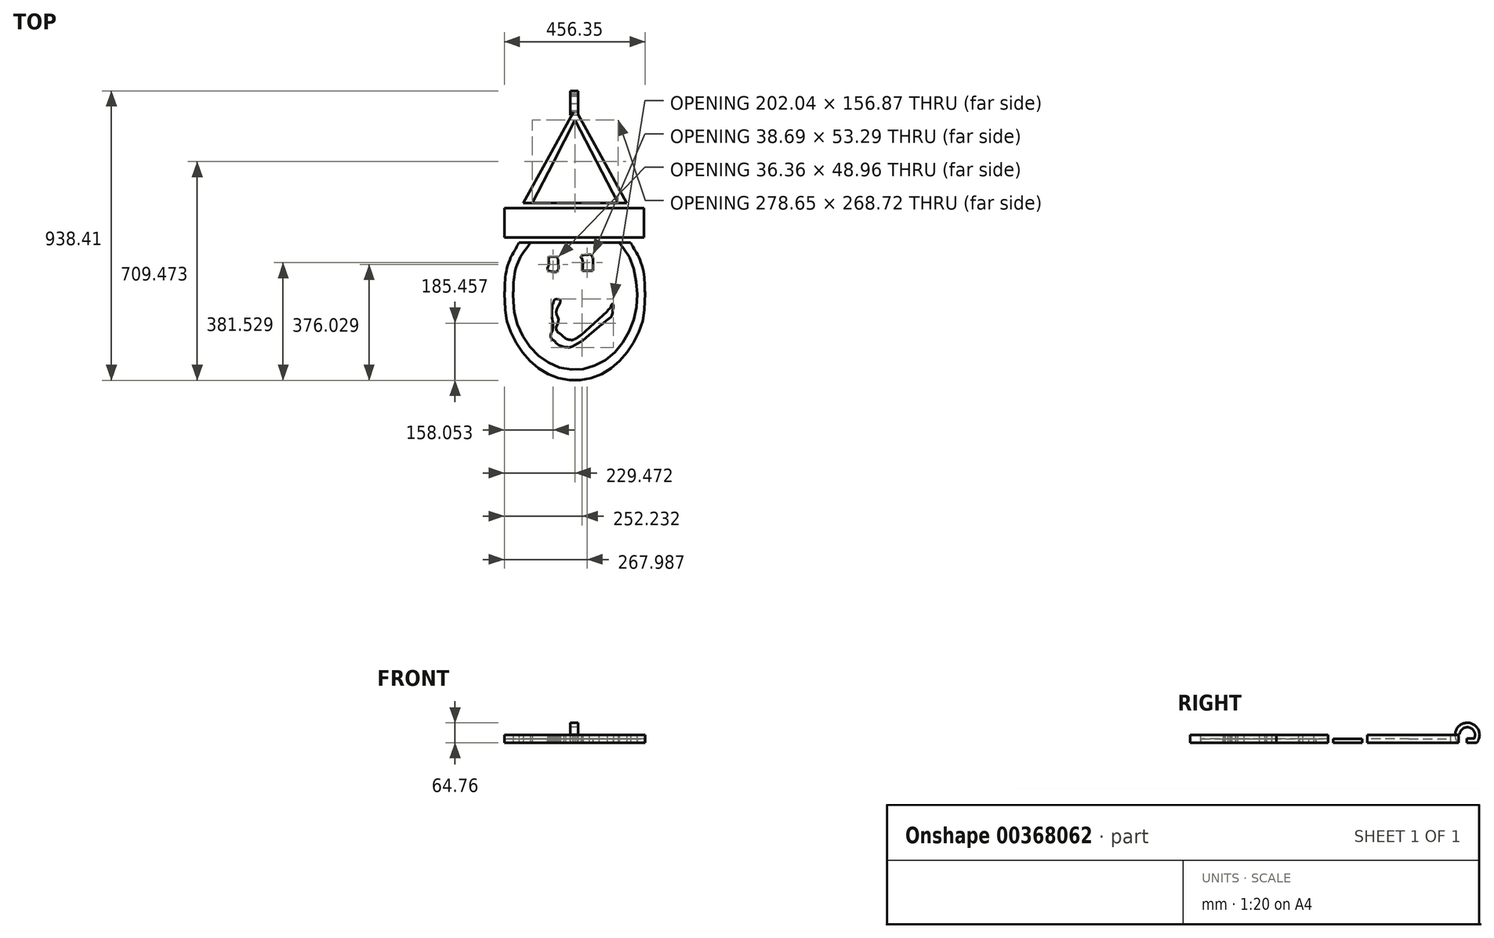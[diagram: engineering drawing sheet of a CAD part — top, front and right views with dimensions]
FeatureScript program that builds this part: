
annotation { "Feature Type Name" : "Feature", "Feature Type Description" : "" }
export const myFeature = defineFeature(function(context is Context, id is Id, definition is map)
    precondition{}
    {
        {
            var Q0;
            Q0=qCreatedBy(makeId("Top.planeOp"),FACE);
            var sketch = newSketch(context, id + "F0", { "sketchPlane" : qUnion([Q0])});
            skFitSpline(sketch, "E0", {"points": [v(-178.82, 5.14) * mm, v(-188.06, -11.68) * mm, v(-206.77, -45.7) * mm, v(-222.61, -102.94) * mm, v(-224.79, -142.5) * mm, v(-225.89, -162.5) * mm]});
            skFitSpline(sketch, "E1", {"points": [v(-225.89, -162.5) * mm, v(-224.4, -186.57) * mm, v(-221.45, -234.01) * mm, v(-198.02, -300.85) * mm, v(-162.12, -358.66) * mm, v(-114.52, -403.46) * mm, v(-58.59, -431.98) * mm, v(1.96, -441.82) * mm, v(62.51, -431.99) * mm, v(118.45, -403.48) * mm, v(166.06, -358.67) * mm, v(201.97, -300.87) * mm, v(225.41, -234.02) * mm, v(228.35, -186.57) * mm, v(229.85, -162.5) * mm]});
            skLineSegment(sketch, "E2", {"start": v(3, 438.57) * mm, "end": v(-88.01, 272.71) * mm});
            skLineSegment(sketch, "E3", {"start": v(-88.01, 272.71) * mm, "end": v(-164.6, 133.21) * mm});
            skLineSegment(sketch, "E4", {"start": v(-164.6, 133.21) * mm, "end": v(170.6, 133.21) * mm});
            skLineSegment(sketch, "E5", {"start": v(170.6, 133.21) * mm, "end": v(94, 272.71) * mm});
            skLineSegment(sketch, "E6", {"start": v(94, 272.71) * mm, "end": v(3, 438.57) * mm});
            skFitSpline(sketch, "E7", {"points": [v(229.85, -162.5) * mm, v(228.74, -142.5) * mm, v(226.54, -102.93) * mm, v(210.65, -45.68) * mm, v(191.92, -11.67) * mm, v(182.66, 5.14) * mm]});
            skFitSpline(sketch, "E8", {"points": [v(-141.9, 5.14) * mm, v(-152.88, -10.94) * mm, v(-175.16, -43.58) * mm, v(-194.2, -101.44) * mm, v(-196.82, -141.96) * mm, v(-198.14, -162.5) * mm]});
            skLineSegment(sketch, "E9", {"start": v(182.66, 5.14) * mm, "end": v(-178.82, 5.14) * mm});
            skLineSegment(sketch, "E10", {"start": v(146.1, 5.14) * mm, "end": v(-141.9, 5.14) * mm});
            skLineSegment(sketch, "E11", {"start": v(-244.23, 133.2) * mm, "end": v(244.23, 133.2) * mm});
            skLineSegment(sketch, "E12", {"start": v(244.23, 133.2) * mm, "end": v(244.23, 5.13) * mm});
            skLineSegment(sketch, "E13", {"start": v(244.23, 5.13) * mm, "end": v(-244.23, 5.13) * mm});
            skLineSegment(sketch, "E14", {"start": v(-244.23, 5.13) * mm, "end": v(-244.23, 133.2) * mm});
            skLineSegment(sketch, "E15", {"start": v(3, 402.01) * mm, "end": v(-66.66, 267.63) * mm});
            skLineSegment(sketch, "E16", {"start": v(-66.66, 267.63) * mm, "end": v(-136.35, 133.3) * mm});
            skLineSegment(sketch, "E17", {"start": v(-136.35, 133.3) * mm, "end": v(3, 133.3) * mm});
            skLineSegment(sketch, "E18", {"start": v(3, 133.3) * mm, "end": v(142.3, 133.3) * mm});
            skLineSegment(sketch, "E19", {"start": v(142.3, 133.3) * mm, "end": v(72.64, 267.63) * mm});
            skLineSegment(sketch, "E20", {"start": v(72.64, 267.63) * mm, "end": v(3, 402.01) * mm});
            skFitSpline(sketch, "E21", {"points": [v(-198.14, -162.5) * mm, v(-196.83, -183.58) * mm, v(-194.25, -225.14) * mm, v(-173.66, -283.68) * mm, v(-142.13, -334.3) * mm, v(-100.31, -373.54) * mm, v(-51.2, -398.5) * mm, v(1.96, -407.13) * mm, v(55.12, -398.5) * mm, v(104.24, -373.54) * mm, v(146, -334.3) * mm, v(177.74, -283.68) * mm, v(197.56, -225.15) * mm, v(204.33, -162.98) * mm, v(197.62, -101.48) * mm, v(179.39, -43.61) * mm, v(157.1, -10.95) * mm, v(146.1, 5.14) * mm]});
            skLineSegment(sketch, "E22", {"start": v(-226.5, 116.41) * mm, "end": v(226.5, 116.41) * mm});
            skLineSegment(sketch, "E23", {"start": v(226.5, 116.41) * mm, "end": v(226.5, 21.92) * mm});
            skLineSegment(sketch, "E24", {"start": v(226.5, 21.92) * mm, "end": v(-226.5, 21.92) * mm});
            skLineSegment(sketch, "E25", {"start": v(-226.5, 21.92) * mm, "end": v(-226.5, 116.41) * mm});
            skFitSpline(sketch, "E26", {"points": [v(-71.66, -200.42) * mm, v(-71.94, -212.65) * mm, v(-72.5, -237.2) * mm, v(-69, -272.4) * mm, v(-76.01, -299.15) * mm, v(-68.45, -311.04) * mm, v(-65.86, -312.06) * mm, v(-64.26, -312.62) * mm, v(-63.72, -312.81) * mm]});
            skLineSegment(sketch, "E27", {"start": v(-63.72, -312.81) * mm, "end": v(-59.91, -319.8) * mm});
            skLineSegment(sketch, "E28", {"start": v(-59.91, -319.8) * mm, "end": v(-50.07, -327.74) * mm});
            skLineSegment(sketch, "E29", {"start": v(-50.07, -327.74) * mm, "end": v(-34.83, -333.13) * mm});
            skFitSpline(sketch, "E30", {"points": [v(-34.83, -333.13) * mm, v(-33.6, -333.3) * mm, v(-29.71, -333.82) * mm, v(-23.14, -334.36) * mm, v(-16.21, -334.74) * mm, v(-10.73, -333.23) * mm, v(-7.3, -331.99) * mm, v(-5.3, -331.17) * mm, v(-4.67, -330.91) * mm]});
            skLineSegment(sketch, "E31", {"start": v(-4.67, -330.91) * mm, "end": v(27.4, -312.81) * mm});
            skLineSegment(sketch, "E32", {"start": v(27.4, -312.81) * mm, "end": v(48.67, -294.72) * mm});
            skLineSegment(sketch, "E33", {"start": v(48.67, -294.72) * mm, "end": v(79.79, -267.41) * mm});
            skFitSpline(sketch, "E34", {"points": [v(79.79, -267.41) * mm, v(82.5, -265.39) * mm, v(91.18, -258.9) * mm, v(104.89, -246.87) * mm, v(118.4, -237.07) * mm, v(122.95, -228.35) * mm, v(123.54, -225.7) * mm, v(124.3, -221.52) * mm, v(124.9, -213.63) * mm, v(127.37, -205.92) * mm, v(123.77, -193.2) * mm, v(116.46, -207.45) * mm, v(110.83, -212.2) * mm, v(107.26, -216.52) * mm, v(106.14, -217.88) * mm]});
            skLineSegment(sketch, "E35", {"start": v(22.95, -294.4) * mm, "end": v(106.14, -217.88) * mm});
            skFitSpline(sketch, "E36", {"points": [v(22.95, -294.4) * mm, v(21.22, -295.63) * mm, v(15.75, -299.5) * mm, v(6.22, -305.16) * mm, v(-4.93, -310.77) * mm, v(-15.64, -309.76) * mm, v(-22.86, -308.13) * mm, v(-27.13, -306.87) * mm, v(-28.48, -306.46) * mm]});
            skLineSegment(sketch, "E37", {"start": v(-49.75, -287.41) * mm, "end": v(-28.48, -306.46) * mm});
            skLineSegment(sketch, "E38", {"start": v(-71.66, -200.42) * mm, "end": v(-71.66, -200.42) * mm});
            skFitSpline(sketch, "E39", {"points": [v(-49.75, -287.41) * mm, v(-50.13, -287.17) * mm, v(-51.3, -286.41) * mm, v(-53.14, -285.07) * mm, v(-58.78, -272.71) * mm, v(-50.72, -245.96) * mm, v(-58.35, -217.05) * mm, v(-44.36, -182.66) * mm, v(-62.11, -179.12) * mm, v(-67.63, -189.78) * mm, v(-70.34, -196.95) * mm, v(-71.66, -200.42) * mm]});
            skFitSpline(sketch, "E40", {"points": [v(-82.64, -41.41) * mm, v(-82.78, -44.11) * mm, v(-83.2, -52.6) * mm, v(-82.1, -65.84) * mm, v(-86.54, -80.83) * mm, v(-77.66, -87.97) * mm, v(-68.6, -89.97) * mm, v(-61.3, -90.16) * mm, v(-57.36, -90.27) * mm]});
            skLineSegment(sketch, "E41", {"start": v(-53.63, -41.31) * mm, "end": v(-82.64, -41.41) * mm});
            skLineSegment(sketch, "E42", {"start": v(-82.64, -41.41) * mm, "end": v(-53.63, -41.31) * mm});
            skLineSegment(sketch, "E43", {"start": v(-53.63, -41.31) * mm, "end": v(-50.27, -76.5) * mm});
            skFitSpline(sketch, "E44", {"points": [v(-57.36, -90.27) * mm, v(-55.98, -88.39) * mm, v(-53.4, -84.9) * mm, v(-51.41, -80.05) * mm, v(-50.53, -77.33) * mm, v(-50.27, -76.5) * mm]});
            skLineSegment(sketch, "E45", {"start": v(26.34, -86.93) * mm, "end": v(28.77, -57.47) * mm});
            skLineSegment(sketch, "E46", {"start": v(28.77, -57.47) * mm, "end": v(26.34, -86.93) * mm});
            skFitSpline(sketch, "E47", {"points": [v(28.77, -57.47) * mm, v(28.4, -56.44) * mm, v(27.21, -53.13) * mm, v(25.58, -47.26) * mm, v(21.54, -43.14) * mm, v(21.64, -39.45) * mm, v(23.06, -38.65) * mm, v(27.12, -36.43) * mm, v(35.48, -34.82) * mm, v(44.37, -34.94) * mm, v(51.25, -33.15) * mm, v(55.1, -36.2) * mm, v(58.93, -41.61) * mm, v(60.78, -52.34) * mm, v(60.63, -65.53) * mm, v(60.56, -77.34) * mm, v(60.35, -84.32) * mm, v(60.28, -86.5) * mm]});
            skLineSegment(sketch, "E48", {"start": v(60.28, -86.5) * mm, "end": v(26.34, -86.93) * mm});
            skLineSegment(sketch, "E49", {"start": v(26.34, -86.93) * mm, "end": v(60.28, -86.5) * mm});
            skSolve(sketch);
        }
        {
            var Q0;
            Q0=makeQuery(id+"F0.imprint","IMPRINT",FACE,{"disambiguationData":[TD([[makeQuery(id+"F0.imprint","IMPRINT",EDGE,{"derivedFrom":sQuery(id+"F0.wireOp",EDGE,"E40")}),1.0]])]});
            var Q1;
            Q1=makeQuery(id+"F0.imprint","IMPRINT",FACE,{"disambiguationData":[TD([[makeQuery(id+"F0.imprint","IMPRINT",EDGE,{"derivedFrom":sQuery(id+"F0.wireOp",EDGE,"E46")}),1.0]])]});
            var Q2;
            {var subQ0=sQuery(id+"F0.wireOp",EDGE,"E26");Q2=makeQuery(id+"F0.imprint","IMPRINT",FACE,{"disambiguationData":[TD([[makeQuery(id+"F0.imprint","IMPRINT",EDGE,{"derivedFrom":subQ0}),1.0]])]});}
            var Q3;
            {var subQ1=sQuery(id+"F0.wireOp",EDGE,"E1");Q3=makeQuery(id+"F0.imprint","IMPRINT",FACE,{"disambiguationData":[TD([[makeQuery(id+"F0.imprint","IMPRINT",EDGE,{"derivedFrom":subQ1}),1.0]])]});}
            var Q4;
            {var subQ7=sQuery(id+"F0.wireOp",EDGE,"E10");Q4=makeQuery(id+"F0.imprint","IMPRINT",FACE,{"disambiguationData":[TD([[makeQuery(id+"F0.imprint","IMPRINT",EDGE,{"derivedFrom":subQ7}),-1.0]])]});}
            var Q5;
            Q5=makeQuery(id+"F0.imprint","IMPRINT",FACE,{"disambiguationData":[TD([[makeQuery(id+"F0.imprint","IMPRINT",EDGE,{"derivedFrom":sQuery(id+"F0.wireOp",EDGE,"E2")}),1.0]])]});
            extrude(context, id + "F1", {"entities" : qUnion([Q0, Q1, Q2, Q3, Q4, Q5]), "depth" : 25.4 * mm});
        }
        {
            var Q0;
            {var subQ1=sQuery(id+"F0.wireOp",EDGE,"E26");Q0=makeQuery(id+"F0.imprint","IMPRINT",FACE,{"disambiguationData":[TD([[makeQuery(id+"F0.imprint","IMPRINT",EDGE,{"derivedFrom":subQ1}),-1.0]])]});}
            var Q1;
            Q1=makeQuery(id+"F0.imprint","IMPRINT",FACE,{"disambiguationData":[TD([[makeQuery(id+"F0.imprint","IMPRINT",EDGE,{"derivedFrom":sQuery(id+"F0.wireOp",EDGE,"E22")}),-1.0]])]});
            var Q2;
            Q2=makeQuery(id+"F0.imprint","IMPRINT",FACE,{"disambiguationData":[TD([[makeQuery(id+"F0.imprint","IMPRINT",EDGE,{"derivedFrom":sQuery(id+"F0.wireOp",EDGE,"E15")}),1.0]])]});
            extrude(context, id + "F2", {"entities" : qUnion([Q0, Q1, Q2]), "depth" : 12.7 * mm});
        }
        {
            var Q0;
            Q0=qCreatedBy(makeId("Right.planeOp"),FACE);
            var sketch = newSketch(context, id + "F3", { "sketchPlane" : qUnion([Q0])});
            skLineSegment(sketch, "E50", {"start": v(404.06, 0) * mm, "end": v(487.65, 0) * mm});
            skLineSegment(sketch, "E51", {"start": v(487.65, 0) * mm, "end": v(525.72, 0) * mm});
            skArc(sketch, "E52", {"start": v(487.65, 0) * mm, "mid": v(456.93, 64.76) * mm, "end": v(426.22, 0) * mm});
            skLineSegment(sketch, "E53", {"start": v(434.54, 13.76) * mm, "end": v(479.32, 13.76) * mm});
            skArc(sketch, "E54", {"start": v(479.32, 13.76) * mm, "mid": v(456.93, 50.2) * mm, "end": v(434.54, 13.76) * mm});
            skSolve(sketch);
        }
        {
            var Q0;
            {var subQ0=sQuery(id+"F3.wireOp",EDGE,"E52");Q0=makeQuery(id+"F3.imprint","IMPRINT",FACE,{"disambiguationData":[TD([[makeQuery(id+"F3.imprint","IMPRINT",EDGE,{"derivedFrom":subQ0}),1.0]])]});}
            extrude(context, id + "F4", {"entities" : qUnion([Q0]), "endBound" : BoundingType.SYMMETRIC, "depth" : 25.4 * mm});
        }
        {
            var Q0;
            Q0=qCreatedBy(makeId("Right.planeOp"),FACE);
            var sketch = newSketch(context, id + "F5", { "sketchPlane" : qUnion([Q0])});
            skLineSegment(sketch, "E55.bottom", {"start": v(455.44, 0) * mm, "end": v(428.3, 0) * mm});
            skLineSegment(sketch, "E55.top", {"start": v(455.44, 27.33) * mm, "end": v(428.3, 27.33) * mm});
            skLineSegment(sketch, "E55.left", {"start": v(455.44, 0) * mm, "end": v(455.44, 27.33) * mm});
            skLineSegment(sketch, "E55.right", {"start": v(428.3, 0) * mm, "end": v(428.3, 27.33) * mm});
            skSolve(sketch);
        }
        {
            var Q0;
            Q0 = qSketchRegion(id + "F5", true);
            extrude(context, id + "F6", {"entities" : qUnion([Q0]), "operationType" : NewBodyOperationType.REMOVE, "endBound" : BoundingType.SYMMETRIC, "oppositeDirection" : true, "depth" : 25.4 * mm});
        }
    });
